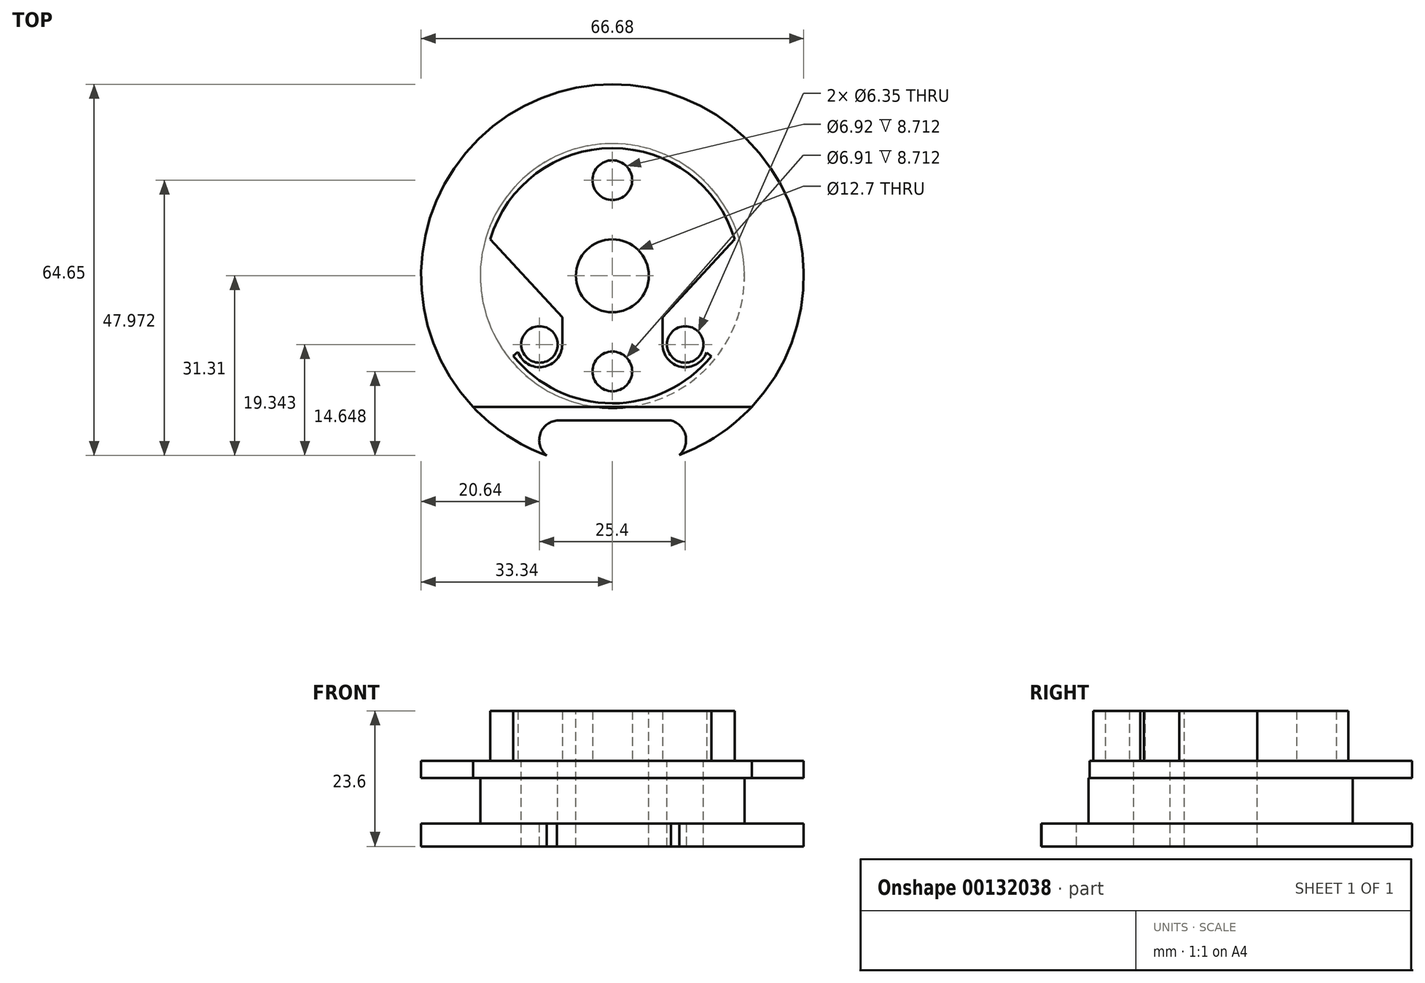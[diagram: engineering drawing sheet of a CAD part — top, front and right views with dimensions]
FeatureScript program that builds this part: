
annotation { "Feature Type Name" : "Feature", "Feature Type Description" : "" }
export const myFeature = defineFeature(function(context is Context, id is Id, definition is map)
    precondition{}
    {
        {
            var Q0;
            Q0=qCreatedBy(makeId("Top.planeOp"),FACE);
            var sketch = newSketch(context, id + "F0", { "sketchPlane" : qUnion([Q0])});
            skLineSegment(sketch, "E0", {"start": v(0, -25.2) * mm, "end": v(-9.68, -25.2) * mm});
            skLineSegment(sketch, "E1", {"start": v(-9.68, -25.2) * mm, "end": v(-8.96, -25.2) * mm});
            skArc(sketch, "E2", {"start": v(-9.68, -25.2) * mm, "mid": v(-12.62, -27.67) * mm, "end": v(-11.44, -31.31) * mm});
            skArc(sketch, "E3.trimOffspring", {"start": v(11.7, -31.22) * mm, "mid": v(12.74, -27.77) * mm, "end": v(10.2, -25.2) * mm});
            skArc(sketch, "E4.trimOffspring", {"start": v(11.7, -31.22) * mm, "mid": v(-0.13, 33.34) * mm, "end": v(-11.44, -31.31) * mm});
            skLineSegment(sketch, "E5.trimOffspring", {"start": v(0, -25.2) * mm, "end": v(10.2, -25.2) * mm});
            skPoint(sketch, "E6.start.orphan", {"position": v(0, -33.34) * mm});
            skSolve(sketch);
        }
        {
            var Q0;
            Q0=makeQuery(id+"F0.imprint","IMPRINT",FACE,{"disambiguationData":[TD([[makeQuery(id+"F0.imprint","IMPRINT",EDGE,{"derivedFrom":sQuery(id+"F0.wireOp",EDGE,"E0")}),-1.0]])]});
            extrude(context, id + "F1", {"entities" : qUnion([Q0]), "depth" : 3.96 * mm});
        }
        {
            var Q0;
            Q0=makeQuery(id+"F1.opExtrude","CAP_FACE",FACE,{"disambiguationData":[OSD([sQuery(id+"F0.wireOp",EDGE,"E0"),sQuery(id+"F0.wireOp",EDGE,"E1"),sQuery(id+"F0.wireOp",EDGE,"E2"),sQuery(id+"F0.wireOp",EDGE,"E3.trimOffspring"),sQuery(id+"F0.wireOp",EDGE,"E4.trimOffspring"),sQuery(id+"F0.wireOp",EDGE,"E5.trimOffspring")])],"isStart":false});
            var sketch = newSketch(context, id + "F2", { "sketchPlane" : qUnion([Q0])});
            skCircle(sketch, "E7", {"center": v(0, 0) * mm, "radius": 23.03 * mm});
            skSolve(sketch);
        }
        {
            var Q0;
            Q0=makeQuery(id+"F2.imprint","IMPRINT",FACE,{"disambiguationData":[TD([[makeQuery(id+"F2.imprint","IMPRINT",EDGE,{"derivedFrom":sQuery(id+"F2.wireOp",EDGE,"E7")}),1.0]])]});
            extrude(context, id + "F3", {"entities" : qUnion([Q0]), "operationType" : NewBodyOperationType.ADD, "depth" : 7.92 * mm});
        }
        {
            var Q0;
            Q0=makeQuery(id+"F3.opExtrude","CAP_FACE",FACE,{"disambiguationData":[OSD([sQuery(id+"F2.wireOp",EDGE,"E7")])],"isStart":false});
            var sketch = newSketch(context, id + "F4", { "sketchPlane" : qUnion([Q0])});
            skArc(sketch, "E8", {"start": v(24.29, -22.84) * mm, "mid": v(0, 33.34) * mm, "end": v(-24.29, -22.84) * mm});
            skLineSegment(sketch, "E9", {"start": v(-24.29, -22.84) * mm, "end": v(24.29, -22.84) * mm});
            skSolve(sketch);
        }
        {
            var Q0;
            Q0 = qSketchRegion(id + "F4", true);
            extrude(context, id + "F5", {"entities" : qUnion([Q0]), "operationType" : NewBodyOperationType.ADD, "depth" : 3 * mm});
        }
        {
            var Q0;
            Q0=makeQuery(id+"F5.opExtrude","CAP_FACE",FACE,{"disambiguationData":[OSD([sQuery(id+"F4.wireOp",EDGE,"E8")])],"isStart":false});
            var sketch = newSketch(context, id + "F6", { "sketchPlane" : qUnion([Q0])});
            skCircle(sketch, "E10", {"center": v(0, 0) * mm, "radius": 22.23 * mm});
            skArc(sketch, "E11", {"start": v(-16.45, -13.24) * mm, "mid": v(-12.06, -15.88) * mm, "end": v(-8.74, -11.97) * mm});
            skArc(sketch, "E12", {"start": v(8.74, -11.97) * mm, "mid": v(11.98, -15.86) * mm, "end": v(16.4, -13.4) * mm});
            skCircle(sketch, "E13", {"center": v(0, 0) * mm, "radius": 6.35 * mm});
            skCircle(sketch, "E14", {"center": v(0, 16.66) * mm, "radius": 3.46 * mm});
            skCircle(sketch, "E15", {"center": v(0, -16.66) * mm, "radius": 3.45 * mm});
            skLineSegment(sketch, "E16", {"start": v(-21.3, 6.35) * mm, "end": v(-8.74, -7.22) * mm});
            skLineSegment(sketch, "E17", {"start": v(21.3, 6.35) * mm, "end": v(8.74, -7.22) * mm});
            skLineSegment(sketch, "E18", {"start": v(8.74, -11.97) * mm, "end": v(8.74, -7.22) * mm});
            skLineSegment(sketch, "E19", {"start": v(-8.74, -11.97) * mm, "end": v(-8.74, -7.22) * mm});
            skPoint(sketch, "E20.orphan", {"position": v(0, 6.35) * mm});
            skLineSegment(sketch, "E21", {"start": v(16.4, -13.4) * mm, "end": v(17.24, -14.03) * mm});
            skLineSegment(sketch, "E22", {"start": v(-16.45, -13.24) * mm, "end": v(-17.27, -13.99) * mm});
            skSolve(sketch);
        }
        {
            var Q0;
            Q0=makeQuery(id+"F6.imprint","IMPRINT",FACE,{"disambiguationData":[TD([[makeQuery(id+"F6.imprint","IMPRINT",EDGE,{"derivedFrom":sQuery(id+"F6.wireOp",EDGE,"E13")}),1.0]])]});
            var Q1;
            Q1=makeQuery(id+"F6.imprint","IMPRINT",FACE,{"disambiguationData":[TD([[makeQuery(id+"F6.imprint","IMPRINT",EDGE,{"derivedFrom":sQuery(id+"F6.wireOp",EDGE,"E11")}),-1.0]])]});
            extrude(context, id + "F7", {"entities" : qUnion([Q0, Q1]), "operationType" : NewBodyOperationType.ADD, "depth" : 8.71 * mm});
        }
        {
            var Q0;
            Q0=makeQuery(id+"F7.opExtrude","CAP_FACE",FACE,{"disambiguationData":[OSD([sQuery(id+"F6.wireOp",EDGE,"E10"),sQuery(id+"F6.wireOp",EDGE,"E11"),sQuery(id+"F6.wireOp",EDGE,"E12"),sQuery(id+"F6.wireOp",EDGE,"E14"),sQuery(id+"F6.wireOp",EDGE,"E15"),sQuery(id+"F6.wireOp",EDGE,"E16"),sQuery(id+"F6.wireOp",EDGE,"E17"),sQuery(id+"F6.wireOp",EDGE,"E18"),sQuery(id+"F6.wireOp",EDGE,"E19"),sQuery(id+"F6.wireOp",EDGE,"E21"),sQuery(id+"F6.wireOp",EDGE,"E22")])],"isStart":false});
            var sketch = newSketch(context, id + "F8", { "sketchPlane" : qUnion([Q0])});
            skCircle(sketch, "E23", {"center": v(0, 0) * mm, "radius": 6.35 * mm});
            skSolve(sketch);
        }
        {
            var Q0;
            Q0 = qSketchRegion(id + "F8", true);
            extrude(context, id + "F9", {"entities" : qUnion([Q0]), "operationType" : NewBodyOperationType.REMOVE, "endBound" : BoundingType.THROUGH_ALL, "oppositeDirection" : true, "depth" : 25.4 * mm});
        }
        {
            var Q0;
            {var subQ1=sQuery(id+"F4.wireOp",EDGE,"E8");Q0=makeQuery(id+"F7.boolean.opBoolean","SPLIT",FACE,{"disambiguationData":[TD([makeQuery(id+"F5.opExtrude","SWEPT_FACE",FACE,{"disambiguationData":[OSD([subQ1])]})])],"derivedFrom":makeQuery(id+"F5.opExtrude","CAP_FACE",FACE,{"disambiguationData":[OSD([subQ1])],"isStart":false})});}
            var sketch = newSketch(context, id + "F10", { "sketchPlane" : qUnion([Q0])});
            skCircle(sketch, "E24", {"center": v(-12.7, -11.97) * mm, "radius": 3.18 * mm});
            skCircle(sketch, "E25", {"center": v(12.7, -11.97) * mm, "radius": 3.18 * mm});
            skSolve(sketch);
        }
        {
            var Q0;
            Q0 = qSketchRegion(id + "F10", true);
            extrude(context, id + "F11", {"entities" : qUnion([Q0]), "operationType" : NewBodyOperationType.REMOVE, "endBound" : BoundingType.THROUGH_ALL, "oppositeDirection" : true, "depth" : 25.4 * mm});
        }
    });
